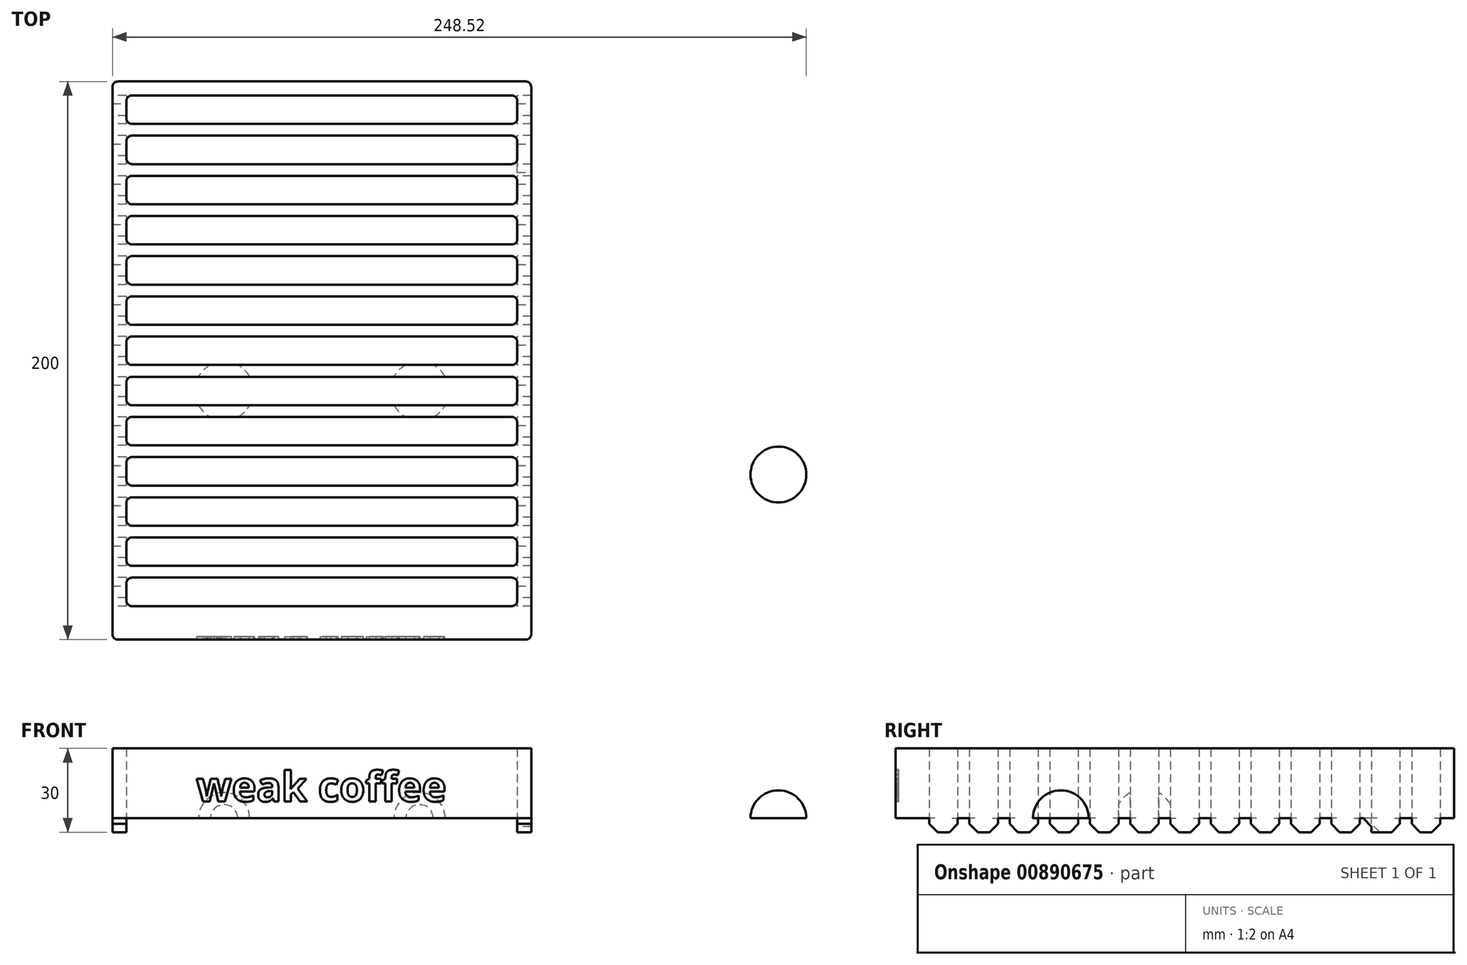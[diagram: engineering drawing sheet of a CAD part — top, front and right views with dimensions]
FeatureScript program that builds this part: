
annotation { "Feature Type Name" : "Feature", "Feature Type Description" : "" }
export const myFeature = defineFeature(function(context is Context, id is Id, definition is map)
    precondition{}
    {
        {
            var Q0;
            Q0=qCreatedBy(makeId("Top.planeOp"),FACE);
            var sketch = newSketch(context, id + "F0", { "sketchPlane" : qUnion([Q0])});
            skLineSegment(sketch, "E0.bottom", {"start": v(-100.51, 220.4) * mm, "end": v(49.49, 220.4) * mm});
            skLineSegment(sketch, "E0.top", {"start": v(-100.51, 20.4) * mm, "end": v(49.49, 20.4) * mm});
            skLineSegment(sketch, "E0.left", {"start": v(-100.51, 220.4) * mm, "end": v(-100.51, 20.4) * mm});
            skLineSegment(sketch, "E0.right", {"start": v(49.49, 220.4) * mm, "end": v(49.49, 20.4) * mm});
            skLineSegment(sketch, "E1.bottom", {"start": v(-95.51, 215.4) * mm, "end": v(44.49, 215.4) * mm});
            skLineSegment(sketch, "E1.top", {"start": v(-95.51, 205.2) * mm, "end": v(44.49, 205.2) * mm});
            skLineSegment(sketch, "E1.left", {"start": v(-95.51, 215.4) * mm, "end": v(-95.51, 205.2) * mm});
            skLineSegment(sketch, "E1.right", {"start": v(44.49, 215.4) * mm, "end": v(44.49, 205.2) * mm});
            skLineSegment(sketch, "E2.0.1.0", {"start": v(-95.51, 190.8) * mm, "end": v(44.49, 190.8) * mm});
            skLineSegment(sketch, "E2.0.1.1", {"start": v(-95.51, 201) * mm, "end": v(44.49, 201) * mm});
            skLineSegment(sketch, "E2.0.1.2", {"start": v(44.49, 201) * mm, "end": v(44.49, 190.8) * mm});
            skLineSegment(sketch, "E2.0.1.3", {"start": v(-95.51, 201) * mm, "end": v(-95.51, 190.8) * mm});
            skLineSegment(sketch, "E2.0.2.0", {"start": v(-95.51, 176.4) * mm, "end": v(44.49, 176.4) * mm});
            skLineSegment(sketch, "E2.0.2.1", {"start": v(-95.51, 186.6) * mm, "end": v(44.49, 186.6) * mm});
            skLineSegment(sketch, "E2.0.2.2", {"start": v(44.49, 186.6) * mm, "end": v(44.49, 176.4) * mm});
            skLineSegment(sketch, "E2.0.2.3", {"start": v(-95.51, 186.6) * mm, "end": v(-95.51, 176.4) * mm});
            skLineSegment(sketch, "E2.0.3.0", {"start": v(-95.51, 162) * mm, "end": v(44.49, 162) * mm});
            skLineSegment(sketch, "E2.0.3.1", {"start": v(-95.51, 172.2) * mm, "end": v(44.49, 172.2) * mm});
            skLineSegment(sketch, "E2.0.3.2", {"start": v(44.49, 172.2) * mm, "end": v(44.49, 162) * mm});
            skLineSegment(sketch, "E2.0.3.3", {"start": v(-95.51, 172.2) * mm, "end": v(-95.51, 162) * mm});
            skLineSegment(sketch, "E2.0.4.0", {"start": v(-95.51, 147.6) * mm, "end": v(44.49, 147.6) * mm});
            skLineSegment(sketch, "E2.0.4.1", {"start": v(-95.51, 157.8) * mm, "end": v(44.49, 157.8) * mm});
            skLineSegment(sketch, "E2.0.4.2", {"start": v(44.49, 157.8) * mm, "end": v(44.49, 147.6) * mm});
            skLineSegment(sketch, "E2.0.4.3", {"start": v(-95.51, 157.8) * mm, "end": v(-95.51, 147.6) * mm});
            skLineSegment(sketch, "E2.0.5.0", {"start": v(-95.51, 133.2) * mm, "end": v(44.49, 133.2) * mm});
            skLineSegment(sketch, "E2.0.5.1", {"start": v(-95.51, 143.4) * mm, "end": v(44.49, 143.4) * mm});
            skLineSegment(sketch, "E2.0.5.2", {"start": v(44.49, 143.4) * mm, "end": v(44.49, 133.2) * mm});
            skLineSegment(sketch, "E2.0.5.3", {"start": v(-95.51, 143.4) * mm, "end": v(-95.51, 133.2) * mm});
            skLineSegment(sketch, "E2.0.6.0", {"start": v(-95.51, 118.8) * mm, "end": v(44.49, 118.8) * mm});
            skLineSegment(sketch, "E2.0.6.1", {"start": v(-95.51, 129) * mm, "end": v(44.49, 129) * mm});
            skLineSegment(sketch, "E2.0.6.2", {"start": v(44.49, 129) * mm, "end": v(44.49, 118.8) * mm});
            skLineSegment(sketch, "E2.0.6.3", {"start": v(-95.51, 129) * mm, "end": v(-95.51, 118.8) * mm});
            skLineSegment(sketch, "E2.0.7.0", {"start": v(-95.51, 104.4) * mm, "end": v(44.49, 104.4) * mm});
            skLineSegment(sketch, "E2.0.7.1", {"start": v(-95.51, 114.6) * mm, "end": v(44.49, 114.6) * mm});
            skLineSegment(sketch, "E2.0.7.2", {"start": v(44.49, 114.6) * mm, "end": v(44.49, 104.4) * mm});
            skLineSegment(sketch, "E2.0.7.3", {"start": v(-95.51, 114.6) * mm, "end": v(-95.51, 104.4) * mm});
            skLineSegment(sketch, "E2.0.8.0", {"start": v(-95.51, 90) * mm, "end": v(44.49, 90) * mm});
            skLineSegment(sketch, "E2.0.8.1", {"start": v(-95.51, 100.2) * mm, "end": v(44.49, 100.2) * mm});
            skLineSegment(sketch, "E2.0.8.2", {"start": v(44.49, 100.2) * mm, "end": v(44.49, 90) * mm});
            skLineSegment(sketch, "E2.0.8.3", {"start": v(-95.51, 100.2) * mm, "end": v(-95.51, 90) * mm});
            skLineSegment(sketch, "E2.0.9.0", {"start": v(-95.51, 75.6) * mm, "end": v(44.49, 75.6) * mm});
            skLineSegment(sketch, "E2.0.9.1", {"start": v(-95.51, 85.8) * mm, "end": v(44.49, 85.8) * mm});
            skLineSegment(sketch, "E2.0.9.2", {"start": v(44.49, 85.8) * mm, "end": v(44.49, 75.6) * mm});
            skLineSegment(sketch, "E2.0.9.3", {"start": v(-95.51, 85.8) * mm, "end": v(-95.51, 75.6) * mm});
            skLineSegment(sketch, "E2.0.10.0", {"start": v(-95.51, 61.2) * mm, "end": v(44.49, 61.2) * mm});
            skLineSegment(sketch, "E2.0.10.1", {"start": v(-95.51, 71.4) * mm, "end": v(44.49, 71.4) * mm});
            skLineSegment(sketch, "E2.0.10.2", {"start": v(44.49, 71.4) * mm, "end": v(44.49, 61.2) * mm});
            skLineSegment(sketch, "E2.0.10.3", {"start": v(-95.51, 71.4) * mm, "end": v(-95.51, 61.2) * mm});
            skLineSegment(sketch, "E2.0.11.0", {"start": v(-95.51, 46.8) * mm, "end": v(44.49, 46.8) * mm});
            skLineSegment(sketch, "E2.0.11.1", {"start": v(-95.51, 57) * mm, "end": v(44.49, 57) * mm});
            skLineSegment(sketch, "E2.0.11.2", {"start": v(44.49, 57) * mm, "end": v(44.49, 46.8) * mm});
            skLineSegment(sketch, "E2.0.11.3", {"start": v(-95.51, 57) * mm, "end": v(-95.51, 46.8) * mm});
            skLineSegment(sketch, "E2.0.12.0", {"start": v(-95.51, 32.4) * mm, "end": v(44.49, 32.4) * mm});
            skLineSegment(sketch, "E2.0.12.1", {"start": v(-95.51, 42.6) * mm, "end": v(44.49, 42.6) * mm});
            skLineSegment(sketch, "E2.0.12.2", {"start": v(44.49, 42.6) * mm, "end": v(44.49, 32.4) * mm});
            skLineSegment(sketch, "E2.0.12.3", {"start": v(-95.51, 42.6) * mm, "end": v(-95.51, 32.4) * mm});
            skLineSegment(sketch, "E2.direction1", {"start": v(-95.51, 205.2) * mm, "end": v(-70.51, 205.2) * mm, "construction": true});
            skLineSegment(sketch, "E2.direction2", {"start": v(-95.51, 205.2) * mm, "end": v(-95.51, 190.8) * mm, "construction": true});
            skSolve(sketch);
        }
        {
            var Q0;
            Q0=makeQuery(id+"F0.imprint","IMPRINT",FACE,{"disambiguationData":[TD([[makeQuery(id+"F0.imprint","IMPRINT",EDGE,{"derivedFrom":sQuery(id+"F0.wireOp",EDGE,"E0.bottom")}),-1.0]])]});
            extrude(context, id + "F1", {"entities" : qUnion([Q0]), "depth" : 25 * mm, "offsetDistance" : 25 * mm});
        }
        {
            var Q0;
            Q0=makeQuery(id+"F1.opExtrude","CAP_FACE",FACE,{"disambiguationData":[OSD([sQuery(id+"F0.wireOp",EDGE,"E0.bottom"),sQuery(id+"F0.wireOp",EDGE,"E0.top"),sQuery(id+"F0.wireOp",EDGE,"E0.left"),sQuery(id+"F0.wireOp",EDGE,"E0.right"),sQuery(id+"F0.wireOp",EDGE,"E1.bottom"),sQuery(id+"F0.wireOp",EDGE,"E1.top"),sQuery(id+"F0.wireOp",EDGE,"E1.left"),sQuery(id+"F0.wireOp",EDGE,"E1.right"),sQuery(id+"F0.wireOp",EDGE,"E2.0.1.0"),sQuery(id+"F0.wireOp",EDGE,"E2.0.1.1"),sQuery(id+"F0.wireOp",EDGE,"E2.0.1.2"),sQuery(id+"F0.wireOp",EDGE,"E2.0.1.3"),sQuery(id+"F0.wireOp",EDGE,"E2.0.2.0"),sQuery(id+"F0.wireOp",EDGE,"E2.0.2.1"),sQuery(id+"F0.wireOp",EDGE,"E2.0.2.2"),sQuery(id+"F0.wireOp",EDGE,"E2.0.2.3"),sQuery(id+"F0.wireOp",EDGE,"E2.0.3.0"),sQuery(id+"F0.wireOp",EDGE,"E2.0.3.1"),sQuery(id+"F0.wireOp",EDGE,"E2.0.3.2"),sQuery(id+"F0.wireOp",EDGE,"E2.0.3.3"),sQuery(id+"F0.wireOp",EDGE,"E2.0.4.0"),sQuery(id+"F0.wireOp",EDGE,"E2.0.4.1"),sQuery(id+"F0.wireOp",EDGE,"E2.0.4.2"),sQuery(id+"F0.wireOp",EDGE,"E2.0.4.3"),sQuery(id+"F0.wireOp",EDGE,"E2.0.5.0"),sQuery(id+"F0.wireOp",EDGE,"E2.0.5.1"),sQuery(id+"F0.wireOp",EDGE,"E2.0.5.2"),sQuery(id+"F0.wireOp",EDGE,"E2.0.5.3"),sQuery(id+"F0.wireOp",EDGE,"E2.0.6.0"),sQuery(id+"F0.wireOp",EDGE,"E2.0.6.1"),sQuery(id+"F0.wireOp",EDGE,"E2.0.6.2"),sQuery(id+"F0.wireOp",EDGE,"E2.0.6.3"),sQuery(id+"F0.wireOp",EDGE,"E2.0.7.0"),sQuery(id+"F0.wireOp",EDGE,"E2.0.7.1"),sQuery(id+"F0.wireOp",EDGE,"E2.0.7.2"),sQuery(id+"F0.wireOp",EDGE,"E2.0.7.3"),sQuery(id+"F0.wireOp",EDGE,"E2.0.8.0"),sQuery(id+"F0.wireOp",EDGE,"E2.0.8.1"),sQuery(id+"F0.wireOp",EDGE,"E2.0.8.2"),sQuery(id+"F0.wireOp",EDGE,"E2.0.8.3"),sQuery(id+"F0.wireOp",EDGE,"E2.0.9.0"),sQuery(id+"F0.wireOp",EDGE,"E2.0.9.1"),sQuery(id+"F0.wireOp",EDGE,"E2.0.9.2"),sQuery(id+"F0.wireOp",EDGE,"E2.0.9.3"),sQuery(id+"F0.wireOp",EDGE,"E2.0.10.0"),sQuery(id+"F0.wireOp",EDGE,"E2.0.10.1"),sQuery(id+"F0.wireOp",EDGE,"E2.0.10.2"),sQuery(id+"F0.wireOp",EDGE,"E2.0.10.3"),sQuery(id+"F0.wireOp",EDGE,"E2.0.11.0"),sQuery(id+"F0.wireOp",EDGE,"E2.0.11.1"),sQuery(id+"F0.wireOp",EDGE,"E2.0.11.2"),sQuery(id+"F0.wireOp",EDGE,"E2.0.11.3"),sQuery(id+"F0.wireOp",EDGE,"E2.0.12.0"),sQuery(id+"F0.wireOp",EDGE,"E2.0.12.1"),sQuery(id+"F0.wireOp",EDGE,"E2.0.12.2"),sQuery(id+"F0.wireOp",EDGE,"E2.0.12.3")])],"isStart":true});
            var sketch = newSketch(context, id + "F2", { "sketchPlane" : qUnion([Q0])});
            skLineSegment(sketch, "E3.bottom", {"start": v(-95.51, -215.4) * mm, "end": v(-100.51, -215.4) * mm});
            skLineSegment(sketch, "E3.top", {"start": v(-95.51, -205.2) * mm, "end": v(-100.51, -205.2) * mm});
            skLineSegment(sketch, "E3.left", {"start": v(-95.51, -215.4) * mm, "end": v(-95.51, -205.2) * mm});
            skLineSegment(sketch, "E3.right", {"start": v(-100.51, -215.4) * mm, "end": v(-100.51, -205.2) * mm});
            skLineSegment(sketch, "E4.0.1.0", {"start": v(-95.51, -190.8) * mm, "end": v(-100.51, -190.8) * mm});
            skLineSegment(sketch, "E4.0.1.1", {"start": v(-95.51, -201) * mm, "end": v(-95.51, -190.8) * mm});
            skLineSegment(sketch, "E4.0.1.2", {"start": v(-100.51, -201) * mm, "end": v(-100.51, -190.8) * mm});
            skLineSegment(sketch, "E4.0.1.3", {"start": v(-95.51, -201) * mm, "end": v(-100.51, -201) * mm});
            skLineSegment(sketch, "E4.0.2.0", {"start": v(-95.51, -176.4) * mm, "end": v(-100.51, -176.4) * mm});
            skLineSegment(sketch, "E4.0.2.1", {"start": v(-95.51, -186.6) * mm, "end": v(-95.51, -176.4) * mm});
            skLineSegment(sketch, "E4.0.2.2", {"start": v(-100.51, -186.6) * mm, "end": v(-100.51, -176.4) * mm});
            skLineSegment(sketch, "E4.0.2.3", {"start": v(-95.51, -186.6) * mm, "end": v(-100.51, -186.6) * mm});
            skLineSegment(sketch, "E4.0.3.0", {"start": v(-95.51, -162) * mm, "end": v(-100.51, -162) * mm});
            skLineSegment(sketch, "E4.0.3.1", {"start": v(-95.51, -172.2) * mm, "end": v(-95.51, -162) * mm});
            skLineSegment(sketch, "E4.0.3.2", {"start": v(-100.51, -172.2) * mm, "end": v(-100.51, -162) * mm});
            skLineSegment(sketch, "E4.0.3.3", {"start": v(-95.51, -172.2) * mm, "end": v(-100.51, -172.2) * mm});
            skLineSegment(sketch, "E4.0.4.0", {"start": v(-95.51, -147.6) * mm, "end": v(-100.51, -147.6) * mm});
            skLineSegment(sketch, "E4.0.4.1", {"start": v(-95.51, -157.8) * mm, "end": v(-95.51, -147.6) * mm});
            skLineSegment(sketch, "E4.0.4.2", {"start": v(-100.51, -157.8) * mm, "end": v(-100.51, -147.6) * mm});
            skLineSegment(sketch, "E4.0.4.3", {"start": v(-95.51, -157.8) * mm, "end": v(-100.51, -157.8) * mm});
            skLineSegment(sketch, "E4.0.5.0", {"start": v(-95.51, -133.2) * mm, "end": v(-100.51, -133.2) * mm});
            skLineSegment(sketch, "E4.0.5.1", {"start": v(-95.51, -143.4) * mm, "end": v(-95.51, -133.2) * mm});
            skLineSegment(sketch, "E4.0.5.2", {"start": v(-100.51, -143.4) * mm, "end": v(-100.51, -133.2) * mm});
            skLineSegment(sketch, "E4.0.5.3", {"start": v(-95.51, -143.4) * mm, "end": v(-100.51, -143.4) * mm});
            skLineSegment(sketch, "E4.0.6.0", {"start": v(-95.51, -118.8) * mm, "end": v(-100.51, -118.8) * mm});
            skLineSegment(sketch, "E4.0.6.1", {"start": v(-95.51, -129) * mm, "end": v(-95.51, -118.8) * mm});
            skLineSegment(sketch, "E4.0.6.2", {"start": v(-100.51, -129) * mm, "end": v(-100.51, -118.8) * mm});
            skLineSegment(sketch, "E4.0.6.3", {"start": v(-95.51, -129) * mm, "end": v(-100.51, -129) * mm});
            skLineSegment(sketch, "E4.0.7.0", {"start": v(-95.51, -104.4) * mm, "end": v(-100.51, -104.4) * mm});
            skLineSegment(sketch, "E4.0.7.1", {"start": v(-95.51, -114.6) * mm, "end": v(-95.51, -104.4) * mm});
            skLineSegment(sketch, "E4.0.7.2", {"start": v(-100.51, -114.6) * mm, "end": v(-100.51, -104.4) * mm});
            skLineSegment(sketch, "E4.0.7.3", {"start": v(-95.51, -114.6) * mm, "end": v(-100.51, -114.6) * mm});
            skLineSegment(sketch, "E4.0.8.0", {"start": v(-95.51, -90) * mm, "end": v(-100.51, -90) * mm});
            skLineSegment(sketch, "E4.0.8.1", {"start": v(-95.51, -100.2) * mm, "end": v(-95.51, -90) * mm});
            skLineSegment(sketch, "E4.0.8.2", {"start": v(-100.51, -100.2) * mm, "end": v(-100.51, -90) * mm});
            skLineSegment(sketch, "E4.0.8.3", {"start": v(-95.51, -100.2) * mm, "end": v(-100.51, -100.2) * mm});
            skLineSegment(sketch, "E4.0.9.0", {"start": v(-95.51, -75.6) * mm, "end": v(-100.51, -75.6) * mm});
            skLineSegment(sketch, "E4.0.9.1", {"start": v(-95.51, -85.8) * mm, "end": v(-95.51, -75.6) * mm});
            skLineSegment(sketch, "E4.0.9.2", {"start": v(-100.51, -85.8) * mm, "end": v(-100.51, -75.6) * mm});
            skLineSegment(sketch, "E4.0.9.3", {"start": v(-95.51, -85.8) * mm, "end": v(-100.51, -85.8) * mm});
            skLineSegment(sketch, "E4.0.10.0", {"start": v(-95.51, -61.2) * mm, "end": v(-100.51, -61.2) * mm});
            skLineSegment(sketch, "E4.0.10.1", {"start": v(-95.51, -71.4) * mm, "end": v(-95.51, -61.2) * mm});
            skLineSegment(sketch, "E4.0.10.2", {"start": v(-100.51, -71.4) * mm, "end": v(-100.51, -61.2) * mm});
            skLineSegment(sketch, "E4.0.10.3", {"start": v(-95.51, -71.4) * mm, "end": v(-100.51, -71.4) * mm});
            skLineSegment(sketch, "E4.0.11.0", {"start": v(-95.51, -46.8) * mm, "end": v(-100.51, -46.8) * mm});
            skLineSegment(sketch, "E4.0.11.1", {"start": v(-95.51, -57) * mm, "end": v(-95.51, -46.8) * mm});
            skLineSegment(sketch, "E4.0.11.2", {"start": v(-100.51, -57) * mm, "end": v(-100.51, -46.8) * mm});
            skLineSegment(sketch, "E4.0.11.3", {"start": v(-95.51, -57) * mm, "end": v(-100.51, -57) * mm});
            skLineSegment(sketch, "E4.0.12.0", {"start": v(-95.51, -32.4) * mm, "end": v(-100.51, -32.4) * mm});
            skLineSegment(sketch, "E4.0.12.1", {"start": v(-95.51, -42.6) * mm, "end": v(-95.51, -32.4) * mm});
            skLineSegment(sketch, "E4.0.12.2", {"start": v(-100.51, -42.6) * mm, "end": v(-100.51, -32.4) * mm});
            skLineSegment(sketch, "E4.0.12.3", {"start": v(-95.51, -42.6) * mm, "end": v(-100.51, -42.6) * mm});
            skLineSegment(sketch, "E4.1.0.0", {"start": v(49.49, -205.2) * mm, "end": v(44.49, -205.2) * mm});
            skLineSegment(sketch, "E4.1.0.1", {"start": v(49.49, -215.4) * mm, "end": v(49.49, -205.2) * mm});
            skLineSegment(sketch, "E4.1.0.2", {"start": v(44.49, -215.4) * mm, "end": v(44.49, -205.2) * mm});
            skLineSegment(sketch, "E4.1.0.3", {"start": v(49.49, -215.4) * mm, "end": v(44.49, -215.4) * mm});
            skLineSegment(sketch, "E4.1.1.0", {"start": v(49.49, -190.8) * mm, "end": v(44.49, -190.8) * mm});
            skLineSegment(sketch, "E4.1.1.1", {"start": v(49.49, -201) * mm, "end": v(49.49, -190.8) * mm});
            skLineSegment(sketch, "E4.1.1.2", {"start": v(44.49, -201) * mm, "end": v(44.49, -190.8) * mm});
            skLineSegment(sketch, "E4.1.1.3", {"start": v(49.49, -201) * mm, "end": v(44.49, -201) * mm});
            skLineSegment(sketch, "E4.1.2.0", {"start": v(49.49, -176.4) * mm, "end": v(44.49, -176.4) * mm});
            skLineSegment(sketch, "E4.1.2.1", {"start": v(49.49, -186.6) * mm, "end": v(49.49, -176.4) * mm});
            skLineSegment(sketch, "E4.1.2.2", {"start": v(44.49, -186.6) * mm, "end": v(44.49, -176.4) * mm});
            skLineSegment(sketch, "E4.1.2.3", {"start": v(49.49, -186.6) * mm, "end": v(44.49, -186.6) * mm});
            skLineSegment(sketch, "E4.1.3.0", {"start": v(49.49, -162) * mm, "end": v(44.49, -162) * mm});
            skLineSegment(sketch, "E4.1.3.1", {"start": v(49.49, -172.2) * mm, "end": v(49.49, -162) * mm});
            skLineSegment(sketch, "E4.1.3.2", {"start": v(44.49, -172.2) * mm, "end": v(44.49, -162) * mm});
            skLineSegment(sketch, "E4.1.3.3", {"start": v(49.49, -172.2) * mm, "end": v(44.49, -172.2) * mm});
            skLineSegment(sketch, "E4.1.4.0", {"start": v(49.49, -147.6) * mm, "end": v(44.49, -147.6) * mm});
            skLineSegment(sketch, "E4.1.4.1", {"start": v(49.49, -157.8) * mm, "end": v(49.49, -147.6) * mm});
            skLineSegment(sketch, "E4.1.4.2", {"start": v(44.49, -157.8) * mm, "end": v(44.49, -147.6) * mm});
            skLineSegment(sketch, "E4.1.4.3", {"start": v(49.49, -157.8) * mm, "end": v(44.49, -157.8) * mm});
            skLineSegment(sketch, "E4.1.5.0", {"start": v(49.49, -133.2) * mm, "end": v(44.49, -133.2) * mm});
            skLineSegment(sketch, "E4.1.5.1", {"start": v(49.49, -143.4) * mm, "end": v(49.49, -133.2) * mm});
            skLineSegment(sketch, "E4.1.5.2", {"start": v(44.49, -143.4) * mm, "end": v(44.49, -133.2) * mm});
            skLineSegment(sketch, "E4.1.5.3", {"start": v(49.49, -143.4) * mm, "end": v(44.49, -143.4) * mm});
            skLineSegment(sketch, "E4.1.6.0", {"start": v(49.49, -118.8) * mm, "end": v(44.49, -118.8) * mm});
            skLineSegment(sketch, "E4.1.6.1", {"start": v(49.49, -129) * mm, "end": v(49.49, -118.8) * mm});
            skLineSegment(sketch, "E4.1.6.2", {"start": v(44.49, -129) * mm, "end": v(44.49, -118.8) * mm});
            skLineSegment(sketch, "E4.1.6.3", {"start": v(49.49, -129) * mm, "end": v(44.49, -129) * mm});
            skLineSegment(sketch, "E4.1.7.0", {"start": v(49.49, -104.4) * mm, "end": v(44.49, -104.4) * mm});
            skLineSegment(sketch, "E4.1.7.1", {"start": v(49.49, -114.6) * mm, "end": v(49.49, -104.4) * mm});
            skLineSegment(sketch, "E4.1.7.2", {"start": v(44.49, -114.6) * mm, "end": v(44.49, -104.4) * mm});
            skLineSegment(sketch, "E4.1.7.3", {"start": v(49.49, -114.6) * mm, "end": v(44.49, -114.6) * mm});
            skLineSegment(sketch, "E4.1.8.0", {"start": v(49.49, -90) * mm, "end": v(44.49, -90) * mm});
            skLineSegment(sketch, "E4.1.8.1", {"start": v(49.49, -100.2) * mm, "end": v(49.49, -90) * mm});
            skLineSegment(sketch, "E4.1.8.2", {"start": v(44.49, -100.2) * mm, "end": v(44.49, -90) * mm});
            skLineSegment(sketch, "E4.1.8.3", {"start": v(49.49, -100.2) * mm, "end": v(44.49, -100.2) * mm});
            skLineSegment(sketch, "E4.1.9.0", {"start": v(49.49, -75.6) * mm, "end": v(44.49, -75.6) * mm});
            skLineSegment(sketch, "E4.1.9.1", {"start": v(49.49, -85.8) * mm, "end": v(49.49, -75.6) * mm});
            skLineSegment(sketch, "E4.1.9.2", {"start": v(44.49, -85.8) * mm, "end": v(44.49, -75.6) * mm});
            skLineSegment(sketch, "E4.1.9.3", {"start": v(49.49, -85.8) * mm, "end": v(44.49, -85.8) * mm});
            skLineSegment(sketch, "E4.1.10.0", {"start": v(49.49, -61.2) * mm, "end": v(44.49, -61.2) * mm});
            skLineSegment(sketch, "E4.1.10.1", {"start": v(49.49, -71.4) * mm, "end": v(49.49, -61.2) * mm});
            skLineSegment(sketch, "E4.1.10.2", {"start": v(44.49, -71.4) * mm, "end": v(44.49, -61.2) * mm});
            skLineSegment(sketch, "E4.1.10.3", {"start": v(49.49, -71.4) * mm, "end": v(44.49, -71.4) * mm});
            skLineSegment(sketch, "E4.1.11.0", {"start": v(49.49, -46.8) * mm, "end": v(44.49, -46.8) * mm});
            skLineSegment(sketch, "E4.1.11.1", {"start": v(49.49, -57) * mm, "end": v(49.49, -46.8) * mm});
            skLineSegment(sketch, "E4.1.11.2", {"start": v(44.49, -57) * mm, "end": v(44.49, -46.8) * mm});
            skLineSegment(sketch, "E4.1.11.3", {"start": v(49.49, -57) * mm, "end": v(44.49, -57) * mm});
            skLineSegment(sketch, "E4.1.12.0", {"start": v(49.49, -32.4) * mm, "end": v(44.49, -32.4) * mm});
            skLineSegment(sketch, "E4.1.12.1", {"start": v(49.49, -42.6) * mm, "end": v(49.49, -32.4) * mm});
            skLineSegment(sketch, "E4.1.12.2", {"start": v(44.49, -42.6) * mm, "end": v(44.49, -32.4) * mm});
            skLineSegment(sketch, "E4.1.12.3", {"start": v(49.49, -42.6) * mm, "end": v(44.49, -42.6) * mm});
            skLineSegment(sketch, "E4.direction1", {"start": v(-100.51, -205.2) * mm, "end": v(44.49, -205.2) * mm, "construction": true});
            skLineSegment(sketch, "E4.direction2", {"start": v(-100.51, -205.2) * mm, "end": v(-100.51, -190.8) * mm, "construction": true});
            skSolve(sketch);
        }
        {
            var Q0;
            Q0 = qSketchRegion(id + "F2", true);
            extrude(context, id + "F3", {"entities" : qUnion([Q0]), "operationType" : NewBodyOperationType.ADD, "depth" : 5 * mm, "offsetDistance" : 25 * mm});
        }
        {
            var Q0;
            Q0=makeQuery(id+"F3.opExtrude","CAP_EDGE",EDGE,{"disambiguationData":[OSD([sQuery(id+"F2.wireOp",EDGE,"E3.bottom")])],"isStart":false});
            var Q1;
            Q1=makeQuery(id+"F3.opExtrude","CAP_EDGE",EDGE,{"disambiguationData":[OSD([sQuery(id+"F2.wireOp",EDGE,"E3.top")])],"isStart":false});
            var Q2;
            Q2=makeQuery(id+"F3.opExtrude","CAP_EDGE",EDGE,{"disambiguationData":[OSD([sQuery(id+"F2.wireOp",EDGE,"E4.0.1.3")])],"isStart":false});
            var Q3;
            Q3=makeQuery(id+"F3.opExtrude","CAP_EDGE",EDGE,{"disambiguationData":[OSD([sQuery(id+"F2.wireOp",EDGE,"E4.0.1.0")])],"isStart":false});
            var Q4;
            Q4=makeQuery(id+"F3.opExtrude","CAP_EDGE",EDGE,{"disambiguationData":[OSD([sQuery(id+"F2.wireOp",EDGE,"E4.0.2.3")])],"isStart":false});
            var Q5;
            Q5=makeQuery(id+"F3.opExtrude","CAP_EDGE",EDGE,{"disambiguationData":[OSD([sQuery(id+"F2.wireOp",EDGE,"E4.0.2.0")])],"isStart":false});
            var Q6;
            Q6=makeQuery(id+"F3.opExtrude","CAP_EDGE",EDGE,{"disambiguationData":[OSD([sQuery(id+"F2.wireOp",EDGE,"E4.0.3.3")])],"isStart":false});
            var Q7;
            Q7=makeQuery(id+"F3.opExtrude","CAP_EDGE",EDGE,{"disambiguationData":[OSD([sQuery(id+"F2.wireOp",EDGE,"E4.0.3.0")])],"isStart":false});
            var Q8;
            Q8=makeQuery(id+"F3.opExtrude","CAP_EDGE",EDGE,{"disambiguationData":[OSD([sQuery(id+"F2.wireOp",EDGE,"E4.0.4.3")])],"isStart":false});
            var Q9;
            Q9=makeQuery(id+"F3.opExtrude","CAP_EDGE",EDGE,{"disambiguationData":[OSD([sQuery(id+"F2.wireOp",EDGE,"E4.0.4.0")])],"isStart":false});
            var Q10;
            Q10=makeQuery(id+"F3.opExtrude","CAP_EDGE",EDGE,{"disambiguationData":[OSD([sQuery(id+"F2.wireOp",EDGE,"E4.0.5.3")])],"isStart":false});
            var Q11;
            Q11=makeQuery(id+"F3.opExtrude","CAP_EDGE",EDGE,{"disambiguationData":[OSD([sQuery(id+"F2.wireOp",EDGE,"E4.0.5.0")])],"isStart":false});
            var Q12;
            Q12=makeQuery(id+"F3.opExtrude","CAP_EDGE",EDGE,{"disambiguationData":[OSD([sQuery(id+"F2.wireOp",EDGE,"E4.0.6.3")])],"isStart":false});
            var Q13;
            Q13=makeQuery(id+"F3.opExtrude","CAP_EDGE",EDGE,{"disambiguationData":[OSD([sQuery(id+"F2.wireOp",EDGE,"E4.0.6.0")])],"isStart":false});
            var Q14;
            Q14=makeQuery(id+"F3.opExtrude","CAP_EDGE",EDGE,{"disambiguationData":[OSD([sQuery(id+"F2.wireOp",EDGE,"E4.0.7.3")])],"isStart":false});
            var Q15;
            Q15=makeQuery(id+"F3.opExtrude","CAP_EDGE",EDGE,{"disambiguationData":[OSD([sQuery(id+"F2.wireOp",EDGE,"E4.0.7.0")])],"isStart":false});
            var Q16;
            Q16=makeQuery(id+"F3.opExtrude","CAP_EDGE",EDGE,{"disambiguationData":[OSD([sQuery(id+"F2.wireOp",EDGE,"E4.0.8.3")])],"isStart":false});
            var Q17;
            Q17=makeQuery(id+"F3.opExtrude","CAP_EDGE",EDGE,{"disambiguationData":[OSD([sQuery(id+"F2.wireOp",EDGE,"E4.0.8.0")])],"isStart":false});
            var Q18;
            Q18=makeQuery(id+"F3.opExtrude","CAP_EDGE",EDGE,{"disambiguationData":[OSD([sQuery(id+"F2.wireOp",EDGE,"E4.0.9.3")])],"isStart":false});
            var Q19;
            Q19=makeQuery(id+"F3.opExtrude","CAP_EDGE",EDGE,{"disambiguationData":[OSD([sQuery(id+"F2.wireOp",EDGE,"E4.0.9.0")])],"isStart":false});
            var Q20;
            Q20=makeQuery(id+"F3.opExtrude","CAP_EDGE",EDGE,{"disambiguationData":[OSD([sQuery(id+"F2.wireOp",EDGE,"E4.0.10.3")])],"isStart":false});
            var Q21;
            Q21=makeQuery(id+"F3.opExtrude","CAP_EDGE",EDGE,{"disambiguationData":[OSD([sQuery(id+"F2.wireOp",EDGE,"E4.0.10.0")])],"isStart":false});
            var Q22;
            Q22=makeQuery(id+"F3.opExtrude","CAP_EDGE",EDGE,{"disambiguationData":[OSD([sQuery(id+"F2.wireOp",EDGE,"E4.0.11.3")])],"isStart":false});
            var Q23;
            Q23=makeQuery(id+"F3.opExtrude","CAP_EDGE",EDGE,{"disambiguationData":[OSD([sQuery(id+"F2.wireOp",EDGE,"E4.0.11.0")])],"isStart":false});
            var Q24;
            Q24=makeQuery(id+"F3.opExtrude","CAP_EDGE",EDGE,{"disambiguationData":[OSD([sQuery(id+"F2.wireOp",EDGE,"E4.0.12.3")])],"isStart":false});
            var Q25;
            Q25=makeQuery(id+"F3.opExtrude","CAP_EDGE",EDGE,{"disambiguationData":[OSD([sQuery(id+"F2.wireOp",EDGE,"E4.0.12.0")])],"isStart":false});
            var Q26;
            Q26=makeQuery(id+"F3.opExtrude","CAP_EDGE",EDGE,{"disambiguationData":[OSD([sQuery(id+"F2.wireOp",EDGE,"E4.1.12.0")])],"isStart":false});
            var Q27;
            Q27=makeQuery(id+"F3.opExtrude","CAP_EDGE",EDGE,{"disambiguationData":[OSD([sQuery(id+"F2.wireOp",EDGE,"E4.1.12.3")])],"isStart":false});
            var Q28;
            Q28=makeQuery(id+"F3.opExtrude","CAP_EDGE",EDGE,{"disambiguationData":[OSD([sQuery(id+"F2.wireOp",EDGE,"E4.1.11.3")])],"isStart":false});
            var Q29;
            Q29=makeQuery(id+"F3.opExtrude","CAP_EDGE",EDGE,{"disambiguationData":[OSD([sQuery(id+"F2.wireOp",EDGE,"E4.1.11.0")])],"isStart":false});
            var Q30;
            Q30=makeQuery(id+"F3.opExtrude","CAP_EDGE",EDGE,{"disambiguationData":[OSD([sQuery(id+"F2.wireOp",EDGE,"E4.1.10.3")])],"isStart":false});
            var Q31;
            Q31=makeQuery(id+"F3.opExtrude","CAP_EDGE",EDGE,{"disambiguationData":[OSD([sQuery(id+"F2.wireOp",EDGE,"E4.1.10.0")])],"isStart":false});
            var Q32;
            Q32=makeQuery(id+"F3.opExtrude","CAP_EDGE",EDGE,{"disambiguationData":[OSD([sQuery(id+"F2.wireOp",EDGE,"E4.1.9.0")])],"isStart":false});
            var Q33;
            Q33=makeQuery(id+"F3.opExtrude","CAP_EDGE",EDGE,{"disambiguationData":[OSD([sQuery(id+"F2.wireOp",EDGE,"E4.1.9.3")])],"isStart":false});
            var Q34;
            Q34=makeQuery(id+"F3.opExtrude","CAP_EDGE",EDGE,{"disambiguationData":[OSD([sQuery(id+"F2.wireOp",EDGE,"E4.1.8.0")])],"isStart":false});
            var Q35;
            Q35=makeQuery(id+"F3.opExtrude","CAP_EDGE",EDGE,{"disambiguationData":[OSD([sQuery(id+"F2.wireOp",EDGE,"E4.1.8.3")])],"isStart":false});
            var Q36;
            Q36=makeQuery(id+"F3.opExtrude","CAP_EDGE",EDGE,{"disambiguationData":[OSD([sQuery(id+"F2.wireOp",EDGE,"E4.1.7.0")])],"isStart":false});
            var Q37;
            Q37=makeQuery(id+"F3.opExtrude","CAP_EDGE",EDGE,{"disambiguationData":[OSD([sQuery(id+"F2.wireOp",EDGE,"E4.1.7.3")])],"isStart":false});
            var Q38;
            Q38=makeQuery(id+"F3.opExtrude","CAP_EDGE",EDGE,{"disambiguationData":[OSD([sQuery(id+"F2.wireOp",EDGE,"E4.1.6.0")])],"isStart":false});
            var Q39;
            Q39=makeQuery(id+"F3.opExtrude","CAP_EDGE",EDGE,{"disambiguationData":[OSD([sQuery(id+"F2.wireOp",EDGE,"E4.1.6.3")])],"isStart":false});
            var Q40;
            Q40=makeQuery(id+"F3.opExtrude","CAP_EDGE",EDGE,{"disambiguationData":[OSD([sQuery(id+"F2.wireOp",EDGE,"E4.1.5.0")])],"isStart":false});
            var Q41;
            Q41=makeQuery(id+"F3.opExtrude","CAP_EDGE",EDGE,{"disambiguationData":[OSD([sQuery(id+"F2.wireOp",EDGE,"E4.1.5.3")])],"isStart":false});
            var Q42;
            Q42=makeQuery(id+"F3.opExtrude","CAP_EDGE",EDGE,{"disambiguationData":[OSD([sQuery(id+"F2.wireOp",EDGE,"E4.1.4.0")])],"isStart":false});
            var Q43;
            Q43=makeQuery(id+"F3.opExtrude","CAP_EDGE",EDGE,{"disambiguationData":[OSD([sQuery(id+"F2.wireOp",EDGE,"E4.1.4.3")])],"isStart":false});
            var Q44;
            Q44=makeQuery(id+"F3.opExtrude","CAP_EDGE",EDGE,{"disambiguationData":[OSD([sQuery(id+"F2.wireOp",EDGE,"E4.1.3.0")])],"isStart":false});
            var Q45;
            Q45=makeQuery(id+"F3.opExtrude","CAP_EDGE",EDGE,{"disambiguationData":[OSD([sQuery(id+"F2.wireOp",EDGE,"E4.1.3.3")])],"isStart":false});
            var Q46;
            Q46=makeQuery(id+"F3.opExtrude","CAP_EDGE",EDGE,{"disambiguationData":[OSD([sQuery(id+"F2.wireOp",EDGE,"E4.1.2.0")])],"isStart":false});
            var Q47;
            Q47=makeQuery(id+"F3.opExtrude","CAP_EDGE",EDGE,{"disambiguationData":[OSD([sQuery(id+"F2.wireOp",EDGE,"E4.1.2.3")])],"isStart":false});
            var Q48;
            Q48=makeQuery(id+"F3.opExtrude","CAP_EDGE",EDGE,{"disambiguationData":[OSD([sQuery(id+"F2.wireOp",EDGE,"E4.1.1.0")])],"isStart":true});
            var Q49;
            Q49=makeQuery(id+"F3.opExtrude","CAP_EDGE",EDGE,{"disambiguationData":[OSD([sQuery(id+"F2.wireOp",EDGE,"E4.1.1.3")])],"isStart":false});
            var Q50;
            Q50=makeQuery(id+"F3.opExtrude","CAP_EDGE",EDGE,{"disambiguationData":[OSD([sQuery(id+"F2.wireOp",EDGE,"E4.1.0.0")])],"isStart":false});
            var Q51;
            Q51=makeQuery(id+"F3.opExtrude","CAP_EDGE",EDGE,{"disambiguationData":[OSD([sQuery(id+"F2.wireOp",EDGE,"E4.1.0.3")])],"isStart":false});
            chamfer(context, id + "F4", {"entities" : qUnion([Q0, Q1, Q2, Q3, Q4, Q5, Q6, Q7, Q8, Q9, Q10, Q11, Q12, Q13, Q14, Q15, Q16, Q17, Q18, Q19, Q20, Q21, Q22, Q23, Q24, Q25, Q26, Q27, Q28, Q29, Q30, Q31, Q32, Q33, Q34, Q35, Q36, Q37, Q38, Q39, Q40, Q41, Q42, Q43, Q44, Q45, Q46, Q47, Q48, Q49, Q50, Q51]), "width" : 3 * mm, "tangentPropagation" : true});
        }
        {
            var Q0;
            {var subQ0=sQuery(id+"F0.wireOp",EDGE,"E1.bottom");var subQ1=sQuery(id+"F0.wireOp",EDGE,"E0.left");var subQ2=sQuery(id+"F0.wireOp",EDGE,"E0.right");var subQ3=sQuery(id+"F0.wireOp",EDGE,"E0.bottom");var subQ4=sQuery(id+"F0.wireOp",EDGE,"E1.left");var subQ5=sQuery(id+"F0.wireOp",EDGE,"E1.right");Q0=makeQuery(id+"F3.boolean.opBoolean","SPLIT",FACE,{"disambiguationData":[TD([makeQuery(id+"F1.opExtrude","SWEPT_FACE",FACE,{"disambiguationData":[OSD([subQ3])]})])],"derivedFrom":makeQuery(id+"F1.opExtrude","CAP_FACE",FACE,{"disambiguationData":[OSD([subQ3,sQuery(id+"F0.wireOp",EDGE,"E0.top"),subQ1,subQ2,subQ0,sQuery(id+"F0.wireOp",EDGE,"E1.top"),subQ4,subQ5,sQuery(id+"F0.wireOp",EDGE,"E2.0.1.0"),sQuery(id+"F0.wireOp",EDGE,"E2.0.1.1"),sQuery(id+"F0.wireOp",EDGE,"E2.0.1.2"),sQuery(id+"F0.wireOp",EDGE,"E2.0.1.3"),sQuery(id+"F0.wireOp",EDGE,"E2.0.2.0"),sQuery(id+"F0.wireOp",EDGE,"E2.0.2.1"),sQuery(id+"F0.wireOp",EDGE,"E2.0.2.2"),sQuery(id+"F0.wireOp",EDGE,"E2.0.2.3"),sQuery(id+"F0.wireOp",EDGE,"E2.0.3.0"),sQuery(id+"F0.wireOp",EDGE,"E2.0.3.1"),sQuery(id+"F0.wireOp",EDGE,"E2.0.3.2"),sQuery(id+"F0.wireOp",EDGE,"E2.0.3.3"),sQuery(id+"F0.wireOp",EDGE,"E2.0.4.0"),sQuery(id+"F0.wireOp",EDGE,"E2.0.4.1"),sQuery(id+"F0.wireOp",EDGE,"E2.0.4.2"),sQuery(id+"F0.wireOp",EDGE,"E2.0.4.3"),sQuery(id+"F0.wireOp",EDGE,"E2.0.5.0"),sQuery(id+"F0.wireOp",EDGE,"E2.0.5.1"),sQuery(id+"F0.wireOp",EDGE,"E2.0.5.2"),sQuery(id+"F0.wireOp",EDGE,"E2.0.5.3"),sQuery(id+"F0.wireOp",EDGE,"E2.0.6.0"),sQuery(id+"F0.wireOp",EDGE,"E2.0.6.1"),sQuery(id+"F0.wireOp",EDGE,"E2.0.6.2"),sQuery(id+"F0.wireOp",EDGE,"E2.0.6.3"),sQuery(id+"F0.wireOp",EDGE,"E2.0.7.0"),sQuery(id+"F0.wireOp",EDGE,"E2.0.7.1"),sQuery(id+"F0.wireOp",EDGE,"E2.0.7.2"),sQuery(id+"F0.wireOp",EDGE,"E2.0.7.3"),sQuery(id+"F0.wireOp",EDGE,"E2.0.8.0"),sQuery(id+"F0.wireOp",EDGE,"E2.0.8.1"),sQuery(id+"F0.wireOp",EDGE,"E2.0.8.2"),sQuery(id+"F0.wireOp",EDGE,"E2.0.8.3"),sQuery(id+"F0.wireOp",EDGE,"E2.0.9.0"),sQuery(id+"F0.wireOp",EDGE,"E2.0.9.1"),sQuery(id+"F0.wireOp",EDGE,"E2.0.9.2"),sQuery(id+"F0.wireOp",EDGE,"E2.0.9.3"),sQuery(id+"F0.wireOp",EDGE,"E2.0.10.0"),sQuery(id+"F0.wireOp",EDGE,"E2.0.10.1"),sQuery(id+"F0.wireOp",EDGE,"E2.0.10.2"),sQuery(id+"F0.wireOp",EDGE,"E2.0.10.3"),sQuery(id+"F0.wireOp",EDGE,"E2.0.11.0"),sQuery(id+"F0.wireOp",EDGE,"E2.0.11.1"),sQuery(id+"F0.wireOp",EDGE,"E2.0.11.2"),sQuery(id+"F0.wireOp",EDGE,"E2.0.11.3"),sQuery(id+"F0.wireOp",EDGE,"E2.0.12.0"),sQuery(id+"F0.wireOp",EDGE,"E2.0.12.1"),sQuery(id+"F0.wireOp",EDGE,"E2.0.12.2"),sQuery(id+"F0.wireOp",EDGE,"E2.0.12.3")])],"isStart":true})});}
            var sketch = newSketch(context, id + "F5", { "sketchPlane" : qUnion([Q0])});
            skLineSegment(sketch, "E5", {"start": v(44.49, -109.5) * mm, "end": v(-95.51, -109.5) * mm, "construction": true});
            skArc(sketch, "E6", {"start": v(19.99, -109.5) * mm, "mid": v(9.49, -99) * mm, "end": v(-1.01, -109.5) * mm});
            skLineSegment(sketch, "E7", {"start": v(-25.51, -114.6) * mm, "end": v(-25.51, -104.4) * mm, "construction": true});
            skArc(sketch, "E8.1.0.0", {"start": v(-50.01, -109.5) * mm, "mid": v(-60.51, -99) * mm, "end": v(-71.01, -109.5) * mm});
            skLineSegment(sketch, "E8.direction1", {"start": v(9.49, -109.5) * mm, "end": v(-60.51, -109.5) * mm, "construction": true});
            skLineSegment(sketch, "E9", {"start": v(-71.01, -109.5) * mm, "end": v(-50.01, -109.5) * mm});
            skLineSegment(sketch, "E10", {"start": v(-1.01, -109.5) * mm, "end": v(19.99, -109.5) * mm});
            skSolve(sketch);
        }
        {
            var Q0;
            Q0=makeQuery(id+"F5.imprint","IMPRINT",FACE,{"disambiguationData":[TD([[makeQuery(id+"F5.imprint","IMPRINT",EDGE,{"derivedFrom":sQuery(id+"F5.wireOp",EDGE,"E6")}),1.0]])]});
            var Q1;
            Q1=makeQuery(id+"F5.imprint","IMPRINT",FACE,{"disambiguationData":[TD([[makeQuery(id+"F5.imprint","IMPRINT",EDGE,{"derivedFrom":sQuery(id+"F5.wireOp",EDGE,"E8.1.0.0")}),1.0]])]});
            var Q2;
            Q2=sQuery(id+"F5.wireOp",EDGE,"E9");
            revolve(context, id + "F6", {"operationType" : NewBodyOperationType.REMOVE, "surfaceOperationType" : NewSurfaceOperationType.NEW, "entities" : qUnion([Q0, Q1]), "axis" : qUnion([Q2]), "revolveType" : RevolveType.FULL, "oppositeDirection" : true});
        }
        {
            var Q0;
            Q0=makeQuery(id+"F1.opExtrude","SWEPT_EDGE",EDGE,{"disambiguationData":[OSD([sQuery(id+"F0.wireOp",EDGE,"E0.top"),sQuery(id+"F0.wireOp",EDGE,"E0.left")])]});
            var Q1;
            Q1=makeQuery(id+"F1.opExtrude","SWEPT_EDGE",EDGE,{"disambiguationData":[OSD([sQuery(id+"F0.wireOp",EDGE,"E0.top"),sQuery(id+"F0.wireOp",EDGE,"E0.right")])]});
            var Q2;
            Q2=makeQuery(id+"F1.opExtrude","SWEPT_EDGE",EDGE,{"disambiguationData":[OSD([sQuery(id+"F0.wireOp",EDGE,"E0.bottom"),sQuery(id+"F0.wireOp",EDGE,"E0.right")])]});
            var Q3;
            Q3=makeQuery(id+"F1.opExtrude","SWEPT_EDGE",EDGE,{"disambiguationData":[OSD([sQuery(id+"F0.wireOp",EDGE,"E0.bottom"),sQuery(id+"F0.wireOp",EDGE,"E0.left")])]});
            var Q4;
            Q4=makeQuery(id+"F1.opExtrude","SWEPT_EDGE",EDGE,{"disambiguationData":[OSD([sQuery(id+"F0.wireOp",EDGE,"E2.0.2.0"),sQuery(id+"F0.wireOp",EDGE,"E2.0.2.2")])]});
            var Q5;
            Q5=makeQuery(id+"F1.opExtrude","SWEPT_EDGE",EDGE,{"disambiguationData":[OSD([sQuery(id+"F0.wireOp",EDGE,"E2.0.1.0"),sQuery(id+"F0.wireOp",EDGE,"E2.0.1.2")])]});
            var Q6;
            Q6=makeQuery(id+"F1.opExtrude","SWEPT_EDGE",EDGE,{"disambiguationData":[OSD([sQuery(id+"F0.wireOp",EDGE,"E1.top"),sQuery(id+"F0.wireOp",EDGE,"E1.right")])]});
            var Q7;
            Q7=makeQuery(id+"F1.opExtrude","SWEPT_EDGE",EDGE,{"disambiguationData":[OSD([sQuery(id+"F0.wireOp",EDGE,"E2.0.3.0"),sQuery(id+"F0.wireOp",EDGE,"E2.0.3.2")])]});
            var Q8;
            Q8=makeQuery(id+"F1.opExtrude","SWEPT_EDGE",EDGE,{"disambiguationData":[OSD([sQuery(id+"F0.wireOp",EDGE,"E2.0.4.0"),sQuery(id+"F0.wireOp",EDGE,"E2.0.4.2")])]});
            var Q9;
            Q9=makeQuery(id+"F1.opExtrude","SWEPT_EDGE",EDGE,{"disambiguationData":[OSD([sQuery(id+"F0.wireOp",EDGE,"E2.0.5.0"),sQuery(id+"F0.wireOp",EDGE,"E2.0.5.2")])]});
            var Q10;
            Q10=makeQuery(id+"F1.opExtrude","SWEPT_EDGE",EDGE,{"disambiguationData":[OSD([sQuery(id+"F0.wireOp",EDGE,"E2.0.6.0"),sQuery(id+"F0.wireOp",EDGE,"E2.0.6.2")])]});
            var Q11;
            Q11=makeQuery(id+"F1.opExtrude","SWEPT_EDGE",EDGE,{"disambiguationData":[OSD([sQuery(id+"F0.wireOp",EDGE,"E2.0.7.0"),sQuery(id+"F0.wireOp",EDGE,"E2.0.7.2")])]});
            var Q12;
            Q12=makeQuery(id+"F1.opExtrude","SWEPT_EDGE",EDGE,{"disambiguationData":[OSD([sQuery(id+"F0.wireOp",EDGE,"E2.0.8.0"),sQuery(id+"F0.wireOp",EDGE,"E2.0.8.2")])]});
            var Q13;
            Q13=makeQuery(id+"F1.opExtrude","SWEPT_EDGE",EDGE,{"disambiguationData":[OSD([sQuery(id+"F0.wireOp",EDGE,"E2.0.9.0"),sQuery(id+"F0.wireOp",EDGE,"E2.0.9.2")])]});
            var Q14;
            Q14=makeQuery(id+"F1.opExtrude","SWEPT_EDGE",EDGE,{"disambiguationData":[OSD([sQuery(id+"F0.wireOp",EDGE,"E2.0.10.0"),sQuery(id+"F0.wireOp",EDGE,"E2.0.10.2")])]});
            var Q15;
            Q15=makeQuery(id+"F1.opExtrude","SWEPT_EDGE",EDGE,{"disambiguationData":[OSD([sQuery(id+"F0.wireOp",EDGE,"E2.0.11.0"),sQuery(id+"F0.wireOp",EDGE,"E2.0.11.2")])]});
            var Q16;
            Q16=makeQuery(id+"F1.opExtrude","SWEPT_EDGE",EDGE,{"disambiguationData":[OSD([sQuery(id+"F0.wireOp",EDGE,"E2.0.12.0"),sQuery(id+"F0.wireOp",EDGE,"E2.0.12.2")])]});
            var Q17;
            Q17=makeQuery(id+"F1.opExtrude","SWEPT_EDGE",EDGE,{"disambiguationData":[OSD([sQuery(id+"F0.wireOp",EDGE,"E1.bottom"),sQuery(id+"F0.wireOp",EDGE,"E1.right")])]});
            var Q18;
            Q18=makeQuery(id+"F1.opExtrude","SWEPT_EDGE",EDGE,{"disambiguationData":[OSD([sQuery(id+"F0.wireOp",EDGE,"E2.0.1.1"),sQuery(id+"F0.wireOp",EDGE,"E2.0.1.2")])]});
            var Q19;
            Q19=makeQuery(id+"F1.opExtrude","SWEPT_EDGE",EDGE,{"disambiguationData":[OSD([sQuery(id+"F0.wireOp",EDGE,"E2.0.2.1"),sQuery(id+"F0.wireOp",EDGE,"E2.0.2.2")])]});
            var Q20;
            Q20=makeQuery(id+"F1.opExtrude","SWEPT_EDGE",EDGE,{"disambiguationData":[OSD([sQuery(id+"F0.wireOp",EDGE,"E2.0.3.1"),sQuery(id+"F0.wireOp",EDGE,"E2.0.3.2")])]});
            var Q21;
            Q21=makeQuery(id+"F1.opExtrude","SWEPT_EDGE",EDGE,{"disambiguationData":[OSD([sQuery(id+"F0.wireOp",EDGE,"E2.0.4.1"),sQuery(id+"F0.wireOp",EDGE,"E2.0.4.2")])]});
            var Q22;
            Q22=makeQuery(id+"F1.opExtrude","SWEPT_EDGE",EDGE,{"disambiguationData":[OSD([sQuery(id+"F0.wireOp",EDGE,"E2.0.5.1"),sQuery(id+"F0.wireOp",EDGE,"E2.0.5.2")])]});
            var Q23;
            Q23=makeQuery(id+"F1.opExtrude","SWEPT_EDGE",EDGE,{"disambiguationData":[OSD([sQuery(id+"F0.wireOp",EDGE,"E2.0.6.1"),sQuery(id+"F0.wireOp",EDGE,"E2.0.6.2")])]});
            var Q24;
            Q24=makeQuery(id+"F1.opExtrude","SWEPT_EDGE",EDGE,{"disambiguationData":[OSD([sQuery(id+"F0.wireOp",EDGE,"E2.0.7.1"),sQuery(id+"F0.wireOp",EDGE,"E2.0.7.2")])]});
            var Q25;
            Q25=makeQuery(id+"F1.opExtrude","SWEPT_EDGE",EDGE,{"disambiguationData":[OSD([sQuery(id+"F0.wireOp",EDGE,"E2.0.8.1"),sQuery(id+"F0.wireOp",EDGE,"E2.0.8.2")])]});
            var Q26;
            Q26=makeQuery(id+"F1.opExtrude","SWEPT_EDGE",EDGE,{"disambiguationData":[OSD([sQuery(id+"F0.wireOp",EDGE,"E2.0.9.1"),sQuery(id+"F0.wireOp",EDGE,"E2.0.9.2")])]});
            var Q27;
            Q27=makeQuery(id+"F1.opExtrude","SWEPT_EDGE",EDGE,{"disambiguationData":[OSD([sQuery(id+"F0.wireOp",EDGE,"E2.0.10.1"),sQuery(id+"F0.wireOp",EDGE,"E2.0.10.2")])]});
            var Q28;
            Q28=makeQuery(id+"F1.opExtrude","SWEPT_EDGE",EDGE,{"disambiguationData":[OSD([sQuery(id+"F0.wireOp",EDGE,"E2.0.11.1"),sQuery(id+"F0.wireOp",EDGE,"E2.0.11.2")])]});
            var Q29;
            Q29=makeQuery(id+"F1.opExtrude","SWEPT_EDGE",EDGE,{"disambiguationData":[OSD([sQuery(id+"F0.wireOp",EDGE,"E2.0.12.1"),sQuery(id+"F0.wireOp",EDGE,"E2.0.12.2")])]});
            var Q30;
            Q30=makeQuery(id+"F1.opExtrude","SWEPT_EDGE",EDGE,{"disambiguationData":[OSD([sQuery(id+"F0.wireOp",EDGE,"E1.top"),sQuery(id+"F0.wireOp",EDGE,"E1.left")])]});
            var Q31;
            Q31=makeQuery(id+"F1.opExtrude","SWEPT_EDGE",EDGE,{"disambiguationData":[OSD([sQuery(id+"F0.wireOp",EDGE,"E2.0.1.0"),sQuery(id+"F0.wireOp",EDGE,"E2.0.1.3")])]});
            var Q32;
            Q32=makeQuery(id+"F1.opExtrude","SWEPT_EDGE",EDGE,{"disambiguationData":[OSD([sQuery(id+"F0.wireOp",EDGE,"E2.0.2.0"),sQuery(id+"F0.wireOp",EDGE,"E2.0.2.3")])]});
            var Q33;
            Q33=makeQuery(id+"F1.opExtrude","SWEPT_EDGE",EDGE,{"disambiguationData":[OSD([sQuery(id+"F0.wireOp",EDGE,"E2.0.3.0"),sQuery(id+"F0.wireOp",EDGE,"E2.0.3.3")])]});
            var Q34;
            Q34=makeQuery(id+"F1.opExtrude","SWEPT_EDGE",EDGE,{"disambiguationData":[OSD([sQuery(id+"F0.wireOp",EDGE,"E2.0.4.0"),sQuery(id+"F0.wireOp",EDGE,"E2.0.4.3")])]});
            var Q35;
            Q35=makeQuery(id+"F1.opExtrude","SWEPT_EDGE",EDGE,{"disambiguationData":[OSD([sQuery(id+"F0.wireOp",EDGE,"E2.0.5.0"),sQuery(id+"F0.wireOp",EDGE,"E2.0.5.3")])]});
            var Q36;
            Q36=makeQuery(id+"F1.opExtrude","SWEPT_EDGE",EDGE,{"disambiguationData":[OSD([sQuery(id+"F0.wireOp",EDGE,"E2.0.6.0"),sQuery(id+"F0.wireOp",EDGE,"E2.0.6.3")])]});
            var Q37;
            Q37=makeQuery(id+"F1.opExtrude","SWEPT_EDGE",EDGE,{"disambiguationData":[OSD([sQuery(id+"F0.wireOp",EDGE,"E2.0.7.0"),sQuery(id+"F0.wireOp",EDGE,"E2.0.7.3")])]});
            var Q38;
            Q38=makeQuery(id+"F1.opExtrude","SWEPT_EDGE",EDGE,{"disambiguationData":[OSD([sQuery(id+"F0.wireOp",EDGE,"E2.0.8.0"),sQuery(id+"F0.wireOp",EDGE,"E2.0.8.3")])]});
            var Q39;
            Q39=makeQuery(id+"F1.opExtrude","SWEPT_EDGE",EDGE,{"disambiguationData":[OSD([sQuery(id+"F0.wireOp",EDGE,"E2.0.9.0"),sQuery(id+"F0.wireOp",EDGE,"E2.0.9.3")])]});
            var Q40;
            Q40=makeQuery(id+"F1.opExtrude","SWEPT_EDGE",EDGE,{"disambiguationData":[OSD([sQuery(id+"F0.wireOp",EDGE,"E2.0.10.0"),sQuery(id+"F0.wireOp",EDGE,"E2.0.10.3")])]});
            var Q41;
            Q41=makeQuery(id+"F1.opExtrude","SWEPT_EDGE",EDGE,{"disambiguationData":[OSD([sQuery(id+"F0.wireOp",EDGE,"E2.0.11.0"),sQuery(id+"F0.wireOp",EDGE,"E2.0.11.3")])]});
            var Q42;
            Q42=makeQuery(id+"F1.opExtrude","SWEPT_EDGE",EDGE,{"disambiguationData":[OSD([sQuery(id+"F0.wireOp",EDGE,"E2.0.12.0"),sQuery(id+"F0.wireOp",EDGE,"E2.0.12.3")])]});
            var Q43;
            Q43=makeQuery(id+"F1.opExtrude","SWEPT_EDGE",EDGE,{"disambiguationData":[OSD([sQuery(id+"F0.wireOp",EDGE,"E1.bottom"),sQuery(id+"F0.wireOp",EDGE,"E1.left")])]});
            var Q44;
            Q44=makeQuery(id+"F1.opExtrude","SWEPT_EDGE",EDGE,{"disambiguationData":[OSD([sQuery(id+"F0.wireOp",EDGE,"E2.0.1.1"),sQuery(id+"F0.wireOp",EDGE,"E2.0.1.3")])]});
            var Q45;
            Q45=makeQuery(id+"F1.opExtrude","SWEPT_EDGE",EDGE,{"disambiguationData":[OSD([sQuery(id+"F0.wireOp",EDGE,"E2.0.2.1"),sQuery(id+"F0.wireOp",EDGE,"E2.0.2.3")])]});
            var Q46;
            Q46=makeQuery(id+"F1.opExtrude","SWEPT_EDGE",EDGE,{"disambiguationData":[OSD([sQuery(id+"F0.wireOp",EDGE,"E2.0.3.1"),sQuery(id+"F0.wireOp",EDGE,"E2.0.3.3")])]});
            var Q47;
            Q47=makeQuery(id+"F1.opExtrude","SWEPT_EDGE",EDGE,{"disambiguationData":[OSD([sQuery(id+"F0.wireOp",EDGE,"E2.0.4.1"),sQuery(id+"F0.wireOp",EDGE,"E2.0.4.3")])]});
            var Q48;
            Q48=makeQuery(id+"F1.opExtrude","SWEPT_EDGE",EDGE,{"disambiguationData":[OSD([sQuery(id+"F0.wireOp",EDGE,"E2.0.5.1"),sQuery(id+"F0.wireOp",EDGE,"E2.0.5.3")])]});
            var Q49;
            Q49=makeQuery(id+"F1.opExtrude","SWEPT_EDGE",EDGE,{"disambiguationData":[OSD([sQuery(id+"F0.wireOp",EDGE,"E2.0.6.1"),sQuery(id+"F0.wireOp",EDGE,"E2.0.6.3")])]});
            var Q50;
            Q50=makeQuery(id+"F1.opExtrude","SWEPT_EDGE",EDGE,{"disambiguationData":[OSD([sQuery(id+"F0.wireOp",EDGE,"E2.0.7.1"),sQuery(id+"F0.wireOp",EDGE,"E2.0.7.3")])]});
            var Q51;
            Q51=makeQuery(id+"F1.opExtrude","SWEPT_EDGE",EDGE,{"disambiguationData":[OSD([sQuery(id+"F0.wireOp",EDGE,"E2.0.8.1"),sQuery(id+"F0.wireOp",EDGE,"E2.0.8.3")])]});
            var Q52;
            Q52=makeQuery(id+"F1.opExtrude","SWEPT_EDGE",EDGE,{"disambiguationData":[OSD([sQuery(id+"F0.wireOp",EDGE,"E2.0.9.1"),sQuery(id+"F0.wireOp",EDGE,"E2.0.9.3")])]});
            var Q53;
            Q53=makeQuery(id+"F1.opExtrude","SWEPT_EDGE",EDGE,{"disambiguationData":[OSD([sQuery(id+"F0.wireOp",EDGE,"E2.0.10.1"),sQuery(id+"F0.wireOp",EDGE,"E2.0.10.3")])]});
            var Q54;
            Q54=makeQuery(id+"F1.opExtrude","SWEPT_EDGE",EDGE,{"disambiguationData":[OSD([sQuery(id+"F0.wireOp",EDGE,"E2.0.11.1"),sQuery(id+"F0.wireOp",EDGE,"E2.0.11.3")])]});
            var Q55;
            Q55=makeQuery(id+"F1.opExtrude","SWEPT_EDGE",EDGE,{"disambiguationData":[OSD([sQuery(id+"F0.wireOp",EDGE,"E2.0.12.1"),sQuery(id+"F0.wireOp",EDGE,"E2.0.12.3")])]});
            fillet(context, id + "F7", {"entities" : qUnion([Q0, Q1, Q2, Q3, Q4, Q5, Q6, Q7, Q8, Q9, Q10, Q11, Q12, Q13, Q14, Q15, Q16, Q17, Q18, Q19, Q20, Q21, Q22, Q23, Q24, Q25, Q26, Q27, Q28, Q29, Q30, Q31, Q32, Q33, Q34, Q35, Q36, Q37, Q38, Q39, Q40, Q41, Q42, Q43, Q44, Q45, Q46, Q47, Q48, Q49, Q50, Q51, Q52, Q53, Q54, Q55]), "radius" : 2 * mm, "tangentPropagation" : true, "allowEdgeOverflow" : false});
        }
        {
            var Q0;
            Q0=makeQuery(id+"F1.opExtrude","SWEPT_FACE",FACE,{"disambiguationData":[OSD([sQuery(id+"F0.wireOp",EDGE,"E0.top")])]});
            var sketch = newSketch(context, id + "F8", { "sketchPlane" : qUnion([Q0])});
            skText(sketch, "E11", { "text": "weak coffee\n", "fontName": "OpenSans-Bold.ttf"});
            skLineSegment(sketch, "E12", {"start": v(-25.51, 0) * mm, "end": v(-25.51, 6) * mm, "construction": true});
            const initialGuessF8  = {"E11": [-0.07047, 0.006, 1, 0, 0.01071]};
            skSetInitialGuess(sketch, initialGuessF8);
            skSolve(sketch);
        }
        {
            var Q0;
            Q0 = qSketchRegion(id + "F8", true);
            extrude(context, id + "F9", {"entities" : qUnion([Q0]), "operationType" : NewBodyOperationType.REMOVE, "oppositeDirection" : true, "depth" : 1 * mm, "offsetDistance" : 25 * mm});
        }
        {
            var Q0;
            Q0=qCreatedBy(makeId("Top.planeOp"),FACE);
            var sketch = newSketch(context, id + "F10", { "sketchPlane" : qUnion([Q0])});
            skArc(sketch, "E13", {"start": v(148, 79.54) * mm, "mid": v(138, 89.54) * mm, "end": v(128, 79.54) * mm});
            skLineSegment(sketch, "E14", {"start": v(128, 79.54) * mm, "end": v(148, 79.54) * mm});
            skSolve(sketch);
        }
        {
            var Q0;
            Q0=makeQuery(id+"F10.imprint","IMPRINT",FACE,{"disambiguationData":[TD([[makeQuery(id+"F10.imprint","IMPRINT",EDGE,{"derivedFrom":sQuery(id+"F10.wireOp",EDGE,"E13")}),1.0]])]});
            var Q1;
            Q1=sQuery(id+"F10.wireOp",EDGE,"E14");
            revolve(context, id + "F11", {"surfaceOperationType" : NewSurfaceOperationType.NEW, "entities" : qUnion([Q0]), "axis" : qUnion([Q1]), "revolveType" : RevolveType.ONE_DIRECTION, "angle" : 180 * degree});
        }
    });
